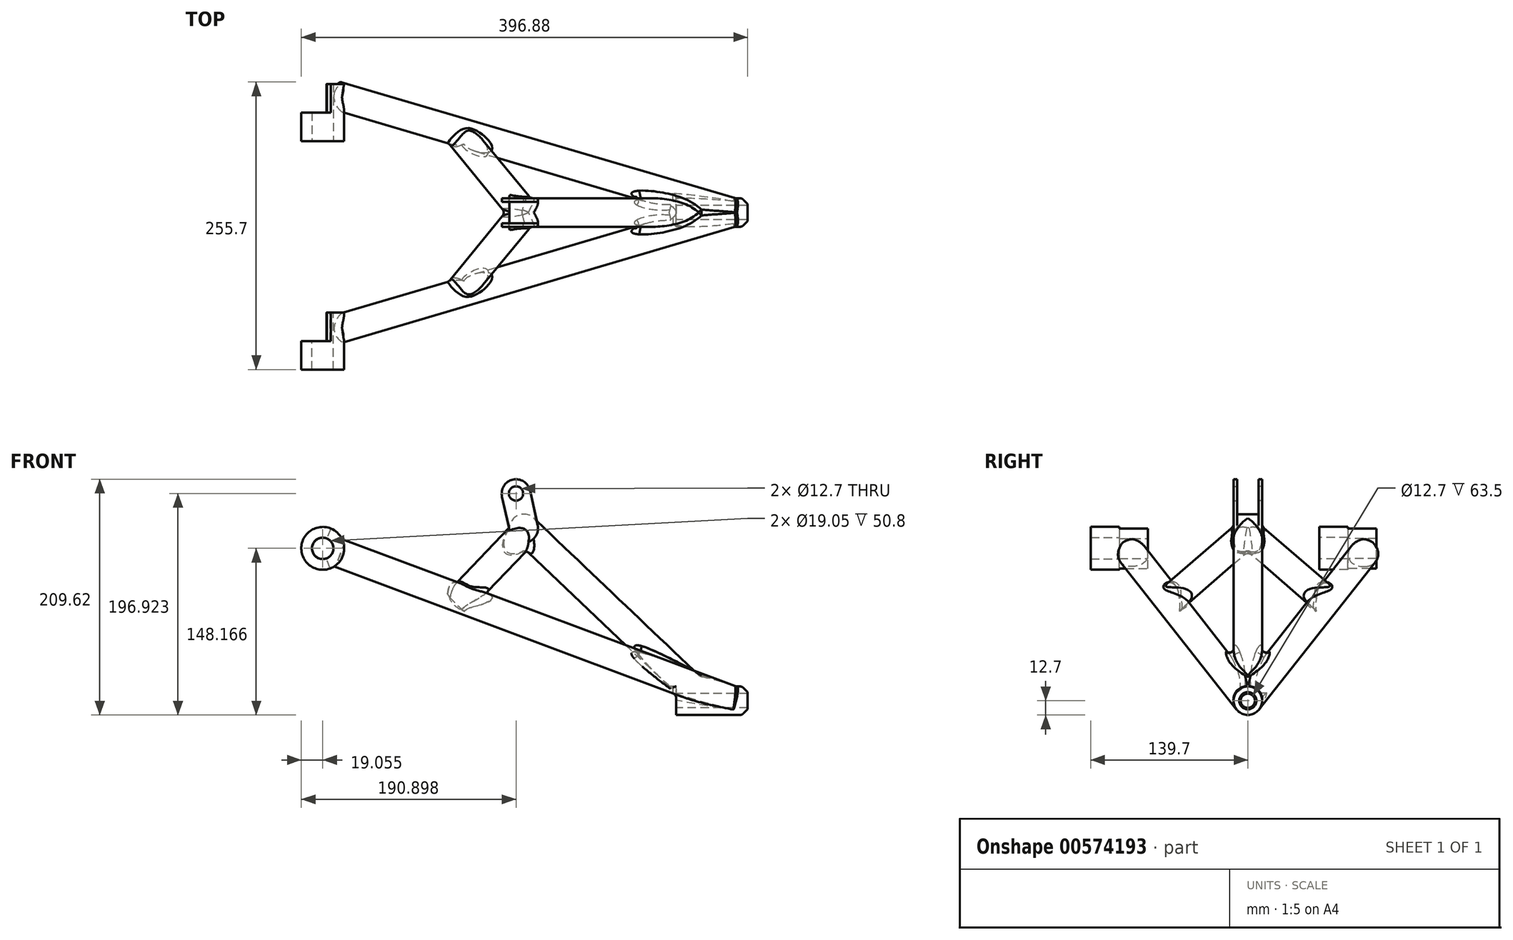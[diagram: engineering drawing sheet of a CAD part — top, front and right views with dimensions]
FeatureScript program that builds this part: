
annotation { "Feature Type Name" : "Feature", "Feature Type Description" : "" }
export const myFeature = defineFeature(function(context is Context, id is Id, definition is map)
    precondition{}
    {
        {
            var Q0;
            Q0=qCreatedBy(makeId("Right.planeOp"),FACE);
            var sketch = newSketch(context, id + "F0", { "sketchPlane" : qUnion([Q0])});
            skCircle(sketch, "E0", {"center": v(0, 0) * mm, "radius": 12.7 * mm});
            skCircle(sketch, "E1", {"center": v(0, 0) * mm, "radius": 6.35 * mm});
            skSolve(sketch);
        }
        {
            var Q0;
            Q0=qSketchRegion(id+"F0",true);
            extrude(context, id + "F1", {"entities" : qUnion([Q0]), "depth" : 12.7 * mm, "offsetDistance" : 25.4 * mm, "hasSecondDirection" : true, "secondDirectionOppositeDirection" : true, "secondDirectionDepth" : 50.8 * mm});
        }
        {
            var Q0;
            Q0=qCreatedBy(makeId("Front.planeOp"),FACE);
            var sketch = newSketch(context, id + "F2", { "sketchPlane" : qUnion([Q0])});
            skCircle(sketch, "E2", {"center": v(-365.13, 135.47) * mm, "radius": 19.05 * mm});
            skCircle(sketch, "E3", {"center": v(-365.13, 135.47) * mm, "radius": 6.35 * mm});
            skLineSegment(sketch, "E4", {"start": v(-365.13, 135.47) * mm, "end": v(-365.13, 0) * mm, "construction": true});
            skLineSegment(sketch, "E5", {"start": v(-348.65, 145.02) * mm, "end": v(-358.6, 117.56) * mm, "construction": true});
            skCircle(sketch, "E6", {"center": v(-365.13, 135.47) * mm, "radius": 9.53 * mm});
            skLineSegment(sketch, "E7", {"start": v(-347.45, 142.56) * mm, "end": v(-356.1, 118.68) * mm, "construction": true});
            skLineSegment(sketch, "E8", {"start": v(-358.6, 117.56) * mm, "end": v(-361.87, 126.52) * mm});
            skLineSegment(sketch, "E9", {"start": v(-357.83, 153.07) * mm, "end": v(-361.48, 144.27) * mm});
            skLineSegment(sketch, "E10", {"start": v(-365.13, 135.47) * mm, "end": v(-401.05, 171.39) * mm, "construction": true});
            skLineSegment(sketch, "E11", {"start": v(-374.65, 135.47) * mm, "end": v(-415.93, 135.47) * mm, "construction": true});
            skLineSegment(sketch, "E12", {"start": v(-365.13, 135.47) * mm, "end": v(-434.55, 0.95) * mm, "construction": true});
            skLineSegment(sketch, "E13", {"start": v(0, 0) * mm, "end": v(-365.13, 135.47) * mm, "construction": true});
            skLineSegment(sketch, "E14", {"start": v(0, 0) * mm, "end": v(-365.13, 0) * mm, "construction": true});
            skLineSegment(sketch, "E15", {"start": v(0, 0) * mm, "end": v(0, 127.83) * mm, "construction": true});
            skCircle(sketch, "E16", {"center": v(-245.53, 91.1) * mm, "radius": 12.7 * mm, "construction": true});
            skLineSegment(sketch, "E17", {"start": v(-365.13, 135.47) * mm, "end": v(-365.13, 406.4) * mm, "construction": true});
            skCircle(sketch, "E18", {"center": v(-365.13, 406.4) * mm, "radius": 6.35 * mm, "construction": true});
            skLineSegment(sketch, "E19", {"start": v(-365.13, 406.4) * mm, "end": v(-50.8, 0) * mm, "construction": true});
            skCircle(sketch, "E20", {"center": v(-193.28, 184.22) * mm, "radius": 6.35 * mm});
            skArc(sketch, "E21", {"start": v(-180.89, 186.98) * mm, "mid": v(-196.04, 196.62) * mm, "end": v(-205.68, 181.46) * mm});
            skPoint(sketch, "E22.trimOffspring.end.orphan", {"position": v(-25.4, 0) * mm});
            skLineSegment(sketch, "E23", {"start": v(-186.38, 153.23) * mm, "end": v(-25.4, 0) * mm, "construction": true});
            skLineSegment(sketch, "E24", {"start": v(-186.38, 153.23) * mm, "end": v(-245.53, 91.1) * mm, "construction": true});
            skCircle(sketch, "E25", {"center": v(-186.38, 153.23) * mm, "radius": 12.7 * mm});
            skLineSegment(sketch, "E26", {"start": v(-198.78, 150.47) * mm, "end": v(-205.68, 181.46) * mm});
            skLineSegment(sketch, "E27", {"start": v(-180.89, 186.98) * mm, "end": v(-173.99, 156) * mm});
            skSolve(sketch);
        }
        {
            var Q0;
            Q0=makeQuery(id+"F2.imprint","IMPRINT",FACE,{"disambiguationData":[TD([[makeQuery(id+"F2.imprint","IMPRINT",EDGE,{"derivedFrom":sQuery(id+"F2.wireOp",EDGE,"E2")}),1.0]])]});
            extrude(context, id + "F3", {"entities" : qUnion([Q0]), "depth" : 139.7 * mm, "offsetDistance" : 25.4 * mm, "hasSecondDirection" : true, "secondDirectionOppositeDirection" : false, "secondDirectionDepth" : 114.3 * mm});
        }
        {
            var Q0;
            {var subQ0=sQuery(id+"F2.wireOp",EDGE,"E8");Q0=makeQuery(id+"F2.imprint","IMPRINT",FACE,{"disambiguationData":[TD([[makeQuery(id+"F2.imprint","IMPRINT",EDGE,{"derivedFrom":subQ0}),-1.0]])]});}
            extrude(context, id + "F4", {"entities" : qUnion([Q0]), "operationType" : NewBodyOperationType.ADD, "depth" : 114.3 * mm, "offsetDistance" : 25.4 * mm, "hasSecondDirection" : true, "secondDirectionOppositeDirection" : false, "secondDirectionDepth" : 88.9 * mm});
        }
        {
            var Q0;
            Q0=qCreatedBy(makeId("Top.planeOp"),FACE);
            cPlane(context, id + "F5", {"entities" : qUnion([Q0]), "cplaneType" : CPlaneType.OFFSET, "offset" : 203.2 * mm, "width" : 152.4 * mm, "height" : 152.4 * mm});
        }
        {
            var Q0;
            Q0=qCreatedBy(makeId("Top.planeOp"),FACE);
            var sketch = newSketch(context, id + "F6", { "sketchPlane" : qUnion([Q0])});
            skLineSegment(sketch, "E28", {"start": v(0, 0) * mm, "end": v(0, -93.22) * mm, "construction": true});
            skLineSegment(sketch, "E29", {"start": v(0, 0) * mm, "end": v(-34.96, -118.66) * mm, "construction": true});
            skLineSegment(sketch, "E30", {"start": v(0, 0) * mm, "end": v(0, 59.23) * mm, "construction": true});
            skLineSegment(sketch, "E31", {"start": v(0, 0) * mm, "end": v(-18.5, 62.77) * mm, "construction": true});
            skSolve(sketch);
        }
        {
            var Q0;
            Q0=sQuery(id+"F6.wireOp",EDGE,"E31");
            cPlane(context, id + "F7", {"entities" : qUnion([Q0]), "cplaneType" : CPlaneType.LINE_ANGLE, "offset" : 25.4 * mm, "angle" : 70.25 * degree, "oppositeDirection" : true, "width" : 152.4 * mm, "height" : 152.4 * mm});
        }
        {
            var Q0;
            Q0=qCreatedBy(id+"F7.planeOp",FACE);
            var sketch = newSketch(context, id + "F8", { "sketchPlane" : qUnion([Q0])});
            skCircle(sketch, "E32", {"center": v(0, 0) * mm, "radius": 12.7 * mm});
            skSolve(sketch);
        }
        {
            var Q0;
            Q0=qSketchRegion(id+"F8",true);
            extrude(context, id + "F9", {"entities" : qUnion([Q0]), "depth" : 390.07 * mm, "offsetDistance" : 25.4 * mm, "hasSecondDirection" : true, "secondDirectionBound" : BoundingType.UP_TO_NEXT, "secondDirectionOppositeDirection" : true, "secondDirectionDepth" : 25.4 * mm});
        }
        {
            var Q0;
            Q0=makeQuery(id+"F2.imprint","IMPRINT",FACE,{"disambiguationData":[TD([[makeQuery(id+"F2.imprint","IMPRINT",EDGE,{"derivedFrom":sQuery(id+"F2.wireOp",EDGE,"E2")}),1.0]])]});
            extrude(context, id + "F10", {"entities" : qUnion([Q0]), "oppositeDirection" : true, "depth" : 88.9 * mm, "offsetDistance" : 25.4 * mm, "hasSecondDirection" : true, "secondDirectionOppositeDirection" : true, "secondDirectionDepth" : 63.5 * mm});
        }
        {
            var Q0;
            {var subQ0=sQuery(id+"F2.wireOp",EDGE,"E8");Q0=makeQuery(id+"F2.imprint","IMPRINT",FACE,{"disambiguationData":[TD([[makeQuery(id+"F2.imprint","IMPRINT",EDGE,{"derivedFrom":subQ0}),-1.0]])]});}
            extrude(context, id + "F11", {"entities" : qUnion([Q0]), "operationType" : NewBodyOperationType.ADD, "oppositeDirection" : true, "depth" : 114.3 * mm, "offsetDistance" : 25.4 * mm, "hasSecondDirection" : true, "secondDirectionOppositeDirection" : true, "secondDirectionDepth" : 88.9 * mm});
        }
        {
            var Q0;
            {var subQ0=sQuery(id+"F0.wireOp",EDGE,"E0");Q0=makeQuery(id+"FOUHgXMMWDp4Atl_3.opBoolean","MERGE",EDGE,{"derivedFrom":[makeQuery(id+"F1.opExtrude","CAP_EDGE",EDGE,{"disambiguationData":[OSD([subQ0])],"isStart":false}),makeQuery(id+"F9.opExtrude","CAP_EDGE",EDGE,{"disambiguationData":[OSD([subQ0])],"isStart":false})]});}
            chamfer(context, id + "F12", {"entities" : qUnion([Q0]), "width" : 5.08 * mm, "tangentPropagation" : true});
        }
        {
            var Q0;
            Q0=sQuery(id+"F2.wireOp",EDGE,"E24");
            cPlane(context, id + "F13", {"entities" : qUnion([Q0]), "cplaneType" : CPlaneType.LINE_ANGLE, "offset" : 25.4 * mm, "angle" : 90 * degree, "width" : 152.4 * mm, "height" : 152.4 * mm});
        }
        {
            var Q0;
            Q0=qCreatedBy(id+"F13.planeOp",FACE);
            var sketch = newSketch(context, id + "F14", { "sketchPlane" : qUnion([Q0])});
            skCircle(sketch, "E33", {"center": v(0, -17.51) * mm, "radius": 12.7 * mm});
            skSolve(sketch);
        }
        {
            var Q0;
            Q0 = qSketchRegion(id + "F14", true);
            var Q1;
            Q1=makeQuery(id+"F1.opExtrude","SWEPT_FACE",FACE,{"disambiguationData":[OSD([sQuery(id+"F0.wireOp",EDGE,"E0")])]});
            extrude(context, id + "F15", {"entities" : qUnion([Q0]), "endBound" : BoundingType.UP_TO_SURFACE, "oppositeDirection" : true, "depth" : 25.4 * mm, "endBoundEntityFace" : qUnion([Q1]), "offsetDistance" : 25.4 * mm, "hasSecondDirection" : true, "secondDirectionOppositeDirection" : false, "secondDirectionDepth" : 12.7 * mm});
        }
        {
            var Q0;
            Q0=sQuery(id+"F2.wireOp",EDGE,"E23");
            cPlane(context, id + "F16", {"entities" : qUnion([Q0]), "cplaneType" : CPlaneType.LINE_ANGLE, "offset" : 25.4 * mm, "angle" : 50 * degree, "width" : 152.4 * mm, "height" : 152.4 * mm});
        }
        {
            var Q0;
            Q0=qCreatedBy(id+"F16.planeOp",FACE);
            var sketch = newSketch(context, id + "F17", { "sketchPlane" : qUnion([Q0])});
            skCircle(sketch, "E34", {"center": v(209.7, 112.99) * mm, "radius": 12.7 * mm});
            skSolve(sketch);
        }
        {
            var Q0;
            Q0 = qSketchRegion(id + "F17", true);
            var Q1;
            Q1=makeQuery(id+"F9.opExtrude","SWEPT_FACE",FACE,{"disambiguationData":[OSD([sQuery(id+"F8.wireOp",EDGE,"E32")])]});
            extrude(context, id + "F18", {"entities" : qUnion([Q0]), "oppositeDirection" : true, "depth" : 107.95 * mm, "endBoundEntityFace" : qUnion([Q1]), "offsetDistance" : 25.4 * mm});
        }
        {
            var Q0;
            Q0=makeQuery(id+"F15.opExtrude","CAP_EDGE",EDGE,{"disambiguationData":[OSD([sQuery(id+"F14.wireOp",EDGE,"E33")])],"isStart":true});
            fillet(context, id + "F19", {"entities" : qUnion([Q0]), "radius" : 12.7 * mm, "tangentPropagation" : true, "allowEdgeOverflow" : false});
        }
        {
            var Q0;
            Q0=makeQuery(id+"F2.imprint","IMPRINT",FACE,{"disambiguationData":[TD([[makeQuery(id+"F2.imprint","IMPRINT",EDGE,{"derivedFrom":sQuery(id+"F2.wireOp",EDGE,"E20")}),-1.0]])]});
            extrude(context, id + "F20", {"entities" : qUnion([Q0]), "depth" : 12.7 * mm, "offsetDistance" : 25.4 * mm, "hasSecondDirection" : true, "secondDirectionOppositeDirection" : false, "secondDirectionDepth" : 9.52 * mm});
        }
        {
            var Q0;
            Q0=makeQuery(id+"F9.opExtrude","SWEPT_BODY",BODY,{"disambiguationData":[OSD([sQuery(id+"F8.wireOp",EDGE,"E32")])]});
            var Q1;
            Q1=makeQuery(id+"F18.opExtrude","SWEPT_BODY",BODY,{"disambiguationData":[OSD([sQuery(id+"F17.wireOp",EDGE,"E34")])]});
            var Q2;
            Q2=makeQuery(id+"F20.opExtrude","SWEPT_BODY",BODY,{"disambiguationData":[OSD([sQuery(id+"F2.wireOp",EDGE,"E20"),sQuery(id+"F2.wireOp",EDGE,"E21"),sQuery(id+"F2.wireOp",EDGE,"E25"),sQuery(id+"F2.wireOp",EDGE,"E26"),sQuery(id+"F2.wireOp",EDGE,"E27")])]});
            var Q3;
            Q3=qCreatedBy(makeId("Front.planeOp"),FACE);
            mirror(context, id + "F21", {"entities" : qUnion([Q0, Q1, Q2]), "mirrorPlane" : qUnion([Q3])});
        }
        {
            var Q0;
            {var subQ0=sQuery(id+"F2.wireOp",EDGE,"E25");var subQ1=makeQuery(id+"F2.imprint","INTERSECT",VERTEX,{"derivedFrom":[subQ0,sQuery(id+"F2.wireOp",EDGE,"E26")]});Q0=makeQuery(id+"F2.imprint","IMPRINT",FACE,{"disambiguationData":[TD([[makeQuery(id+"F2.imprint","IMPRINT",EDGE,{"disambiguationData":[TD([[subQ1,1.0]])],"derivedFrom":subQ0}),1.0]])]});}
            extrude(context, id + "F22", {"entities" : qUnion([Q0]), "depth" : 25.4 * mm, "offsetDistance" : 25.4 * mm, "symmetric" : true});
        }
        {
            var Q0;
            Q0=makeQuery(id+"F22.opExtrude","SWEPT_BODY",BODY,{"disambiguationData":[OSD([sQuery(id+"F2.wireOp",EDGE,"E25")])]});
            var Q1;
            Q1=makeQuery(id+"F21.opPattern","COPY",BODY,{"derivedFrom":makeQuery(id+"F9.opExtrude","SWEPT_BODY",BODY,{"disambiguationData":[OSD([sQuery(id+"F8.wireOp",EDGE,"E32")])]}),"instanceName":"1"});
            var Q2;
            Q2=makeQuery(id+"F9.opExtrude","SWEPT_BODY",BODY,{"disambiguationData":[OSD([sQuery(id+"F8.wireOp",EDGE,"E32")])]});
            var Q3;
            Q3=makeQuery(id+"F10.opExtrude","SWEPT_BODY",BODY,{"disambiguationData":[OSD([sQuery(id+"F2.wireOp",EDGE,"E2"),sQuery(id+"F2.wireOp",EDGE,"E6")])]});
            var Q4;
            Q4=makeQuery(id+"F15.opExtrude","SWEPT_BODY",BODY,{"disambiguationData":[OSD([sQuery(id+"F14.wireOp",EDGE,"E33")])]});
            var Q5;
            Q5=makeQuery(id+"F3.opExtrude","SWEPT_BODY",BODY,{"disambiguationData":[OSD([sQuery(id+"F2.wireOp",EDGE,"E2"),sQuery(id+"F2.wireOp",EDGE,"E6")])]});
            var Q6;
            Q6=makeQuery(id+"F21.opPattern","COPY",BODY,{"derivedFrom":makeQuery(id+"F18.opExtrude","SWEPT_BODY",BODY,{"disambiguationData":[OSD([sQuery(id+"F17.wireOp",EDGE,"E34")])]}),"instanceName":"1"});
            var Q7;
            Q7=makeQuery(id+"F1.opExtrude","SWEPT_BODY",BODY,{"disambiguationData":[OSD([sQuery(id+"F0.wireOp",EDGE,"E0"),sQuery(id+"F0.wireOp",EDGE,"E1")])]});
            var Q8;
            Q8=makeQuery(id+"F18.opExtrude","SWEPT_BODY",BODY,{"disambiguationData":[OSD([sQuery(id+"F17.wireOp",EDGE,"E34")])]});
            var Q9;
            Q9=makeQuery(id+"F20.opExtrude","SWEPT_BODY",BODY,{"disambiguationData":[OSD([sQuery(id+"F2.wireOp",EDGE,"E20"),sQuery(id+"F2.wireOp",EDGE,"E21"),sQuery(id+"F2.wireOp",EDGE,"E25"),sQuery(id+"F2.wireOp",EDGE,"E26"),sQuery(id+"F2.wireOp",EDGE,"E27")])]});
            var Q10;
            Q10=makeQuery(id+"F21.opPattern","COPY",BODY,{"derivedFrom":makeQuery(id+"F20.opExtrude","SWEPT_BODY",BODY,{"disambiguationData":[OSD([sQuery(id+"F2.wireOp",EDGE,"E20"),sQuery(id+"F2.wireOp",EDGE,"E21"),sQuery(id+"F2.wireOp",EDGE,"E25"),sQuery(id+"F2.wireOp",EDGE,"E26"),sQuery(id+"F2.wireOp",EDGE,"E27")])]}),"instanceName":"1"});
            booleanBodies(context, id + "F23", {"operationType" : BooleanOperationType.UNION, "tools" : qUnion([Q0, Q1, Q2, Q3, Q4, Q5, Q6, Q7, Q8, Q9, Q10])});
        }
        {
            var Q0;
            {var subQ0=sQuery(id+"F2.wireOp",EDGE,"E25");Q0=makeQuery(id+"F23.opBoolean","INTERSECT",EDGE,{"derivedFrom":[makeQuery(id+"F18.opExtrude","SWEPT_FACE",FACE,{"disambiguationData":[OSD([sQuery(id+"F17.wireOp",EDGE,"E34")])]}),makeQuery(id+"F20.opExtrude","CAP_FACE",FACE,{"disambiguationData":[OSD([sQuery(id+"F2.wireOp",EDGE,"E20"),sQuery(id+"F2.wireOp",EDGE,"E21"),subQ0,sQuery(id+"F2.wireOp",EDGE,"E26"),sQuery(id+"F2.wireOp",EDGE,"E27")])],"isStart":false}),makeQuery(id+"F22.opExtrude","CAP_FACE",FACE,{"disambiguationData":[OSD([subQ0])],"isStart":false})]});}
            var Q1;
            {var subQ0=sQuery(id+"F2.wireOp",EDGE,"E25");Q1=makeQuery(id+"F23.opBoolean","INTERSECT",EDGE,{"derivedFrom":[makeQuery(id+"F21.opPattern","COPY",FACE,{"derivedFrom":makeQuery(id+"F18.opExtrude","SWEPT_FACE",FACE,{"disambiguationData":[OSD([sQuery(id+"F17.wireOp",EDGE,"E34")])]}),"instanceName":"1"}),makeQuery(id+"F21.opPattern","COPY",FACE,{"derivedFrom":makeQuery(id+"F20.opExtrude","CAP_FACE",FACE,{"disambiguationData":[OSD([sQuery(id+"F2.wireOp",EDGE,"E20"),sQuery(id+"F2.wireOp",EDGE,"E21"),subQ0,sQuery(id+"F2.wireOp",EDGE,"E26"),sQuery(id+"F2.wireOp",EDGE,"E27")])],"isStart":false}),"instanceName":"1"}),makeQuery(id+"F22.opExtrude","CAP_FACE",FACE,{"disambiguationData":[OSD([subQ0])],"isStart":true})]});}
            var Q2;
            {var subQ0=makeQuery(id+"F18.opExtrude","SWEPT_FACE",FACE,{"disambiguationData":[OSD([sQuery(id+"F17.wireOp",EDGE,"E34")])]});Q2=makeQuery(id+"F23.opBoolean","INTERSECT",EDGE,{"disambiguationData":[OD(3.0)],"derivedFrom":[subQ0,makeQuery(id+"F21.opPattern","COPY",FACE,{"derivedFrom":subQ0,"instanceName":"1"})]});}
            var Q3;
            Q3=makeQuery(id+"F23.opBoolean","INTERSECT",EDGE,{"derivedFrom":[makeQuery(id+"F21.opPattern","COPY",FACE,{"derivedFrom":makeQuery(id+"F9.opExtrude","SWEPT_FACE",FACE,{"disambiguationData":[OSD([sQuery(id+"F8.wireOp",EDGE,"E32")])]}),"instanceName":"1"}),makeQuery(id+"F21.opPattern","COPY",FACE,{"derivedFrom":makeQuery(id+"F18.opExtrude","SWEPT_FACE",FACE,{"disambiguationData":[OSD([sQuery(id+"F17.wireOp",EDGE,"E34")])]}),"instanceName":"1"})]});
            var Q4;
            Q4=makeQuery(id+"F23.opBoolean","INTERSECT",EDGE,{"derivedFrom":[makeQuery(id+"F9.opExtrude","SWEPT_FACE",FACE,{"disambiguationData":[OSD([sQuery(id+"F8.wireOp",EDGE,"E32")])]}),makeQuery(id+"F18.opExtrude","SWEPT_FACE",FACE,{"disambiguationData":[OSD([sQuery(id+"F17.wireOp",EDGE,"E34")])]})]});
            fillet(context, id + "F24", {"entities" : qUnion([Q0, Q1, Q2, Q3, Q4]), "radius" : 5.08 * mm, "tangentPropagation" : true, "allowEdgeOverflow" : false});
        }
        {
            var Q0;
            {var subQ0=sQuery(id+"F0.wireOp",EDGE,"E0");var subQ1=makeQuery(id+"F9.opExtrude","CAP_FACE",FACE,{"disambiguationData":[OSD([subQ0])],"isStart":false});Q0=makeQuery(id+"F23.opBoolean","INTERSECT",EDGE,{"disambiguationData":[OD(0.0)],"derivedFrom":[makeQuery(id+"F1.opExtrude","SWEPT_FACE",FACE,{"disambiguationData":[OSD([subQ0])]}),subQ1,makeQuery(id+"F9.opExtrude","SWEPT_FACE",FACE,{"disambiguationData":[OSD([sQuery(id+"F8.wireOp",EDGE,"E32")])]}),makeQuery(id+"F21.opPattern","COPY",FACE,{"derivedFrom":subQ1,"instanceName":"1"})]});}
            var Q1;
            Q1=makeQuery(id+"F23.opBoolean","INTERSECT",EDGE,{"disambiguationData":[OD(0.0)],"derivedFrom":[makeQuery(id+"F1.opExtrude","SWEPT_FACE",FACE,{"disambiguationData":[OSD([sQuery(id+"F0.wireOp",EDGE,"E0")])]}),makeQuery(id+"F21.opPattern","COPY",FACE,{"derivedFrom":makeQuery(id+"F9.opExtrude","SWEPT_FACE",FACE,{"disambiguationData":[OSD([sQuery(id+"F8.wireOp",EDGE,"E32")])]}),"instanceName":"1"})]});
            var Q2;
            Q2=makeQuery(id+"F23.opBoolean","INTERSECT",EDGE,{"disambiguationData":[OD(1.0)],"derivedFrom":[makeQuery(id+"F1.opExtrude","SWEPT_FACE",FACE,{"disambiguationData":[OSD([sQuery(id+"F0.wireOp",EDGE,"E0")])]}),makeQuery(id+"F21.opPattern","COPY",FACE,{"derivedFrom":makeQuery(id+"F9.opExtrude","SWEPT_FACE",FACE,{"disambiguationData":[OSD([sQuery(id+"F8.wireOp",EDGE,"E32")])]}),"instanceName":"1"})]});
            var Q3;
            Q3=makeQuery(id+"F20.opExtrude","CAP_EDGE",EDGE,{"disambiguationData":[OSD([sQuery(id+"F2.wireOp",EDGE,"E25")])],"isStart":true});
            var Q4;
            Q4=makeQuery(id+"F23.opBoolean","INTERSECT",EDGE,{"derivedFrom":[makeQuery(id+"F1.opExtrude","CAP_FACE",FACE,{"disambiguationData":[OSD([sQuery(id+"F0.wireOp",EDGE,"E0"),sQuery(id+"F0.wireOp",EDGE,"E1")])],"isStart":true}),makeQuery(id+"F9.opExtrude","SWEPT_FACE",FACE,{"disambiguationData":[OSD([sQuery(id+"F8.wireOp",EDGE,"E32")])]})]});
            var Q5;
            Q5=makeQuery(id+"F23.opBoolean","INTERSECT",EDGE,{"derivedFrom":[makeQuery(id+"F1.opExtrude","CAP_FACE",FACE,{"disambiguationData":[OSD([sQuery(id+"F0.wireOp",EDGE,"E0"),sQuery(id+"F0.wireOp",EDGE,"E1")])],"isStart":true}),makeQuery(id+"F21.opPattern","COPY",FACE,{"derivedFrom":makeQuery(id+"F9.opExtrude","SWEPT_FACE",FACE,{"disambiguationData":[OSD([sQuery(id+"F8.wireOp",EDGE,"E32")])]}),"instanceName":"1"})]});
            fillet(context, id + "F25", {"entities" : qUnion([Q0, Q1, Q2, Q3, Q4, Q5]), "radius" : 5.08 * mm, "tangentPropagation" : true, "allowEdgeOverflow" : false});
        }
        {
            var Q0;
            {var subQ0=sQuery(id+"F0.wireOp",EDGE,"E0");var subQ1=makeQuery(id+"F12.opChamfer","BLEND_EDGE",EDGE,{"blendedFrom":[makeQuery(id+"F9.opExtrude","CAP_EDGE",EDGE,{"disambiguationData":[OSD([subQ0])],"isStart":false}),makeQuery(id+"F9.opExtrude","CAP_FACE",FACE,{"disambiguationData":[OSD([subQ0])],"isStart":false})],"blendedInto":[makeQuery(id+"F9.opExtrude","CAP_FACE",FACE,{"disambiguationData":[OSD([subQ0])],"isStart":false})]});Q0=makeQuery(id+"F23.opBoolean","MERGE",EDGE,{"derivedFrom":[makeQuery(id+"F12.opChamfer","BLEND_EDGE",EDGE,{"blendedFrom":[makeQuery(id+"F1.opExtrude","CAP_EDGE",EDGE,{"disambiguationData":[OSD([subQ0])],"isStart":false}),makeQuery(id+"F1.opExtrude","SWEPT_FACE",FACE,{"disambiguationData":[OSD([subQ0])]})],"blendedInto":[makeQuery(id+"F1.opExtrude","SWEPT_FACE",FACE,{"disambiguationData":[OSD([subQ0])]})]}),subQ1,makeQuery(id+"F21.opPattern","COPY",EDGE,{"derivedFrom":subQ1,"instanceName":"1"})]});}
            var Q1;
            Q1=makeQuery(id+"F23.opBoolean","INTERSECT",EDGE,{"derivedFrom":[makeQuery(id+"F9.opExtrude","SWEPT_FACE",FACE,{"disambiguationData":[OSD([sQuery(id+"F8.wireOp",EDGE,"E32")])]}),makeQuery(id+"F15.opExtrude","SWEPT_FACE",FACE,{"disambiguationData":[OSD([sQuery(id+"F14.wireOp",EDGE,"E33")])]})]});
            var Q2;
            Q2=makeQuery(id+"F23.opBoolean","INTERSECT",EDGE,{"derivedFrom":[makeQuery(id+"F15.opExtrude","SWEPT_FACE",FACE,{"disambiguationData":[OSD([sQuery(id+"F14.wireOp",EDGE,"E33")])]}),makeQuery(id+"F21.opPattern","COPY",FACE,{"derivedFrom":makeQuery(id+"F9.opExtrude","SWEPT_FACE",FACE,{"disambiguationData":[OSD([sQuery(id+"F8.wireOp",EDGE,"E32")])]}),"instanceName":"1"})]});
            var Q3;
            {var subQ0=makeQuery(id+"F9.opExtrude","SWEPT_FACE",FACE,{"disambiguationData":[OSD([sQuery(id+"F8.wireOp",EDGE,"E32")])]});Q3=makeQuery(id+"F23.opBoolean","INTERSECT",EDGE,{"derivedFrom":[subQ0,makeQuery(id+"F21.opPattern","COPY",FACE,{"derivedFrom":subQ0,"instanceName":"1"})]});}
            var Q4;
            Q4=makeQuery(id+"F21.opPattern","COPY",EDGE,{"derivedFrom":makeQuery(id+"F20.opExtrude","CAP_EDGE",EDGE,{"disambiguationData":[OSD([sQuery(id+"F2.wireOp",EDGE,"E25")])],"isStart":true}),"instanceName":"1"});
            fillet(context, id + "F26", {"entities" : qUnion([Q0, Q1, Q2, Q3, Q4]), "radius" : 5.08 * mm, "tangentPropagation" : true, "allowEdgeOverflow" : false});
        }
        {
            var Q0;
            Q0=makeQuery(id+"F23.opBoolean","INTERSECT",EDGE,{"derivedFrom":[makeQuery(id+"F18.opExtrude","SWEPT_FACE",FACE,{"disambiguationData":[OSD([sQuery(id+"F17.wireOp",EDGE,"E34")])]}),makeQuery(id+"F15.opExtrude","SWEPT_FACE",FACE,{"disambiguationData":[OSD([sQuery(id+"F14.wireOp",EDGE,"E33")])]})]});
            fillet(context, id + "F27", {"entities" : qUnion([Q0]), "radius" : 5.08 * mm, "tangentPropagation" : true, "allowEdgeOverflow" : false});
        }
    });
